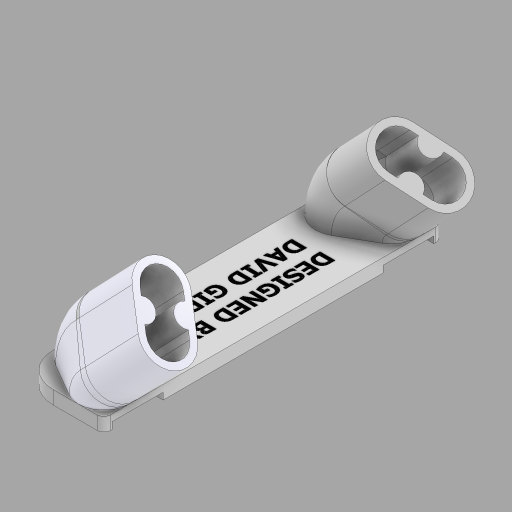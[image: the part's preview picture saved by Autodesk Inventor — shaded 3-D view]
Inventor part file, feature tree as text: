
AUTODESK INVENTOR PART (.ipt)
format: ipt  version: 2023 (Build 270158000, 158)  size: 1,077,760 bytes
history: native  units: mm
features: extrude x17, sketch x12, plane x2, revolve x2, chamfer x2, fillet x2, sweep x1, mirror x1
ambient origin geometry x8: Origin, YZ Plane, XZ Plane, XY Plane, X Axis, Y Axis, Z Axis, Center Point
bodies: Solid1 (feature_tree)
feature tree (39):
  sketch  "Sketch1"  dims[d0=100.0mm d1=25.0mm d2=7.5mm d3=7.5mm d4=60.0deg d5=15.0mm d6=11.0mm d7=11.0mm d8=15.0mm d11=135.0deg]
  plane  "Work Plane1"
  sweep  "Sweep1"
  extrude  "Extrusion1"  Depth=4.0mm TaperAngle=0.0deg
  revolve  "Revolution1"  Angle=45.0deg
  sketch  "Sketch6"  dims[d31=10.0mm d32=45.0deg]
  extrude  "Extrusion4"  TaperAngle=45.0deg  [1 undecoded]
  extrude  "Extrusion5"  Depth=10.0mm
  sketch  "Sketch7"  dims[d33=10.0mm d34=10.0mm]
  extrude  "Extrusion6"  Depth=10.0mm
  extrude  "Extrusion7"  Depth=15.0mm
  mirror  "Mirror4"
  plane  "Work Plane9"
  extrude  "Extrusion8"  Depth=5.5mm
  revolve  "Revolution2"  [1 undecoded]
  extrude  "Extrusion9"  Depth=6.5mm
  sketch  "Sketch19"  dims[d60=5.5mm d61=5.5mm]
  extrude  "Extrusion10"  Depth=20.0mm TaperAngle=0.0deg
  extrude  "Extrusion11"  Depth=10.0mm
  extrude  "Extrusion12"  TaperAngle=90.0deg  [1 undecoded]
  sketch  "Sketch21"  dims[d65=2.0mm d66=6.5mm]
  extrude  "Extrusion13"  Depth=10.0mm
  chamfer  "Chamfer3"  Distance=5.5mm
  extrude  "Extrusion15"  Depth=10.0mm
  extrude  "Extrusion18"  Depth=10.0mm
  fillet  "Fillet2"  Radius=11.0mm
  fillet  "Fillet3"  Radius=11.0mm
  extrude  "Extrusion19"  Depth=10.0mm
  extrude  "Extrusion20"  Depth=10.0mm
  extrude  "Extrusion21"  Depth=10.0mm
  extrude  "Extrusion22"  Depth=10.0mm TaperAngle=0.0deg
  chamfer  "Chamfer5"  Distance=10.0mm
  sketch  "Sketch3"  dims[d12=0.0mm d13=0.0mm d14=4.0mm d15=0.0mm]
  sketch  "Sketch5"  dims[d29=11.389087mm d30=45.0deg]
  sketch  "Sketch14"  dims[d35=45.0deg d37=10.0mm]
  sketch  "Sketch15"  dims[d38=0.977384mm d57=15.0mm]
  sketch  "Sketch20"  dims[d63=11.0mm d64=11.0mm]
  sketch  "Sketch22"  dims[d67=6.5mm d68=20.0mm d69=0.0mm]
  sketch  "Sketch23"  dims[d70=325.0mm d71=0.0mm d72=7.5mm d73=90.0deg d74=7.5mm d75=5.5mm d76=5.5mm d77=15.0mm d78=11.0mm d79=11.0mm d80=2.0mm d81=6.5mm d82=6.5mm d83=10.0mm d84=0.0mm d93=10.0mm d94=0.0mm d115=20.0mm d116=0.0mm d131=8.726646mm d132=300.0mm d133=0.0mm d134=15.0mm d135=300.0mm d136=0.0mm d137=11.0mm d138=11.0mm d139=2.0mm d140=6.5mm d141=6.5mm d142=10.0mm d143=0.0mm d144=40.0mm d145=0.0mm d146=25.0mm d147=100.0mm d150=15.0mm d151=5.5mm d152=2.0mm d153=0.0mm d156=2.0mm d157=4.0mm d158=45.0deg d162=549.891mm d163=50.0mm d164=100.0mm d167=2.5mm d169=15.0mm d170=17.5mm d171=17.5mm d174=10.0mm d175=300.0mm d176=0.0mm d177=7.5mm d183=2.0mm d184=0.0mm d185=2.0mm d186=10.0mm d187=3.0mm d188=0.0mm d189=15.0mm d190=0.0mm d191=1.0mm d192=0.0mm d193=6.5mm d194=10.0mm d195=0.0mm d196=2.0mm d197=4.0mm d198=45.0deg d178=0.872665mm]
note: 3 required parameter values undecoded (feature->parameter linkage not recoverable at this tier; creation-order binding heuristic only, values carry confidence <= 0.55)